# Revit family: Resideo_Thermostat_T4a
name_source: partatom
category: Electrical Fixtures
units: mm (PartAtom-declared; Revit-internal decimal feet)

## family parameters
Cut with Voids When Loaded = No
Host = Face
Maintain Annotation Orientation = No
OmniClass Number = 23.75.65.11.11
OmniClass Title = Heating Controllers
Part Type = Normal
Room Calculation Point = No
Round Connector Dimension = Use Diameter
Shared = No

## types (3) — shared parameters
Assembly Code = D3060
AssetType = Fixed
BIMObjectName = Resideo_Thermostat_T4
ClassificationName = Uniclass2015
ClassificationValue = Pr_75_50_76_73
DisplayMaterial = Resideo - Screen - Green
DocumentationCertificates = https://www.bimstore.co
DocumentationInstallationGuide = https://www.bimstore.co
DocumentationLiterature = https://www.bimstore.co
DocumentationMaintenance = https://www.bimstore.co
DocumentationTechnical = https://www.bimstore.co
DurationUnit = Years
IfcExportAs = IfcUnitaryControlElement
IfcExportType = IfcUnitaryControlElementTypeEnum.CONTROLPANEL
Keynote = W
Manufacturer = Resideo
ManufacturerName = Resideo
NBSDescription = Room temperature sensors
NBSObjectName = Resideo - Room temperature sensors
NominalDepth = 28 mm  [stored 0.0918635 ft]
NominalHeight = 97 mm  [stored 0.318241 ft]
NominalLength = 136 mm
PrimaryMaterial = Resideo - Plastic - White
ProductionYear = 2022
SecondaryMaterial = Resideo - Plastic - Dark Grey
Size = 28mm (D) x 97mm (H) x 136mm (L)
URL = https://www.resideo.com
WarrantyDurationLabor = 0
WarrantyDurationParts = 0
WarrantyDurationUnit = Years
WarrantyGuarantorLabor = https://www.resideo.com
WarrantyGuarantorParts = https://www.resideo.com
_BSBibleVersion = 16
_CurrentRevision = 1
_DistributedBy = https://www.bimstore.co
_ObjectUserGuide = https://www.bimstore.co
zero-valued in all types: Cost, Default Elevation, ExpectedLife, _BimSpecGuid

## per-type parameters (varying)
| type | Description | ModelReference | Type Comments | TypeName |
| T4H110A1021 | T4 WIRED PROGRAMMABLE THERMOSTAT | T4 WIRED PROGRAMMABLE THERMOSTAT | T4 WIRED PROGRAMMABLE THERMOSTAT | T4H110A1021 - T4 WIRED PROGRAMMABLE THERMOSTAT |
| T4H110A1013 | T4 FOR WEST EUROPE | T4 FOR WEST EUROPE | T4 FOR WEST EUROPE | T4H110A1013 - T4 FOR WEST EUROPE |
| T4H110A1023 | T4 FOR WEST EUROPE | T4 FOR WEST EUROPE | T4 FOR WEST EUROPE | T4H110A1023 - T4 FOR WEST EUROPE |

note: column(s) folded — value = type name in every type: Model, ModelNumber

note: [stored X ft] marks values corroborated as IEEE doubles in the binary element streams (Revit-internal decimal feet)

## geometry (parser evidence)
native form markers: Sweep x3
no freeform markers — native parametric forms only
